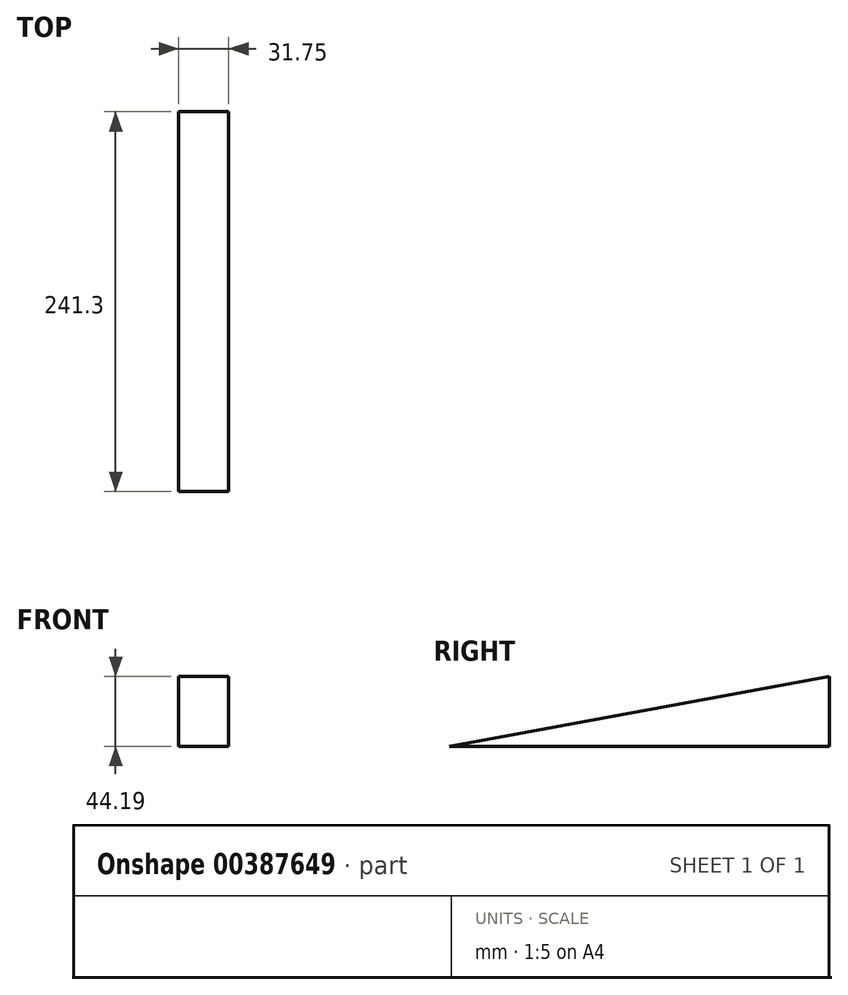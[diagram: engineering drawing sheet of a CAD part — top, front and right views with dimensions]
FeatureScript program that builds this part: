
annotation { "Feature Type Name" : "Feature", "Feature Type Description" : "" }
export const myFeature = defineFeature(function(context is Context, id is Id, definition is map)
    precondition{}
    {
        {
            var Q0;
            Q0=qCreatedBy(makeId("Right.planeOp"),FACE);
            var sketch = newSketch(context, id + "F0", { "sketchPlane" : qUnion([Q0])});
            skLineSegment(sketch, "E0", {"start": v(151.84, 46.52) * mm, "end": v(151.84, 2.33) * mm});
            skLineSegment(sketch, "E1", {"start": v(151.84, 2.33) * mm, "end": v(-89.46, 2.33) * mm});
            skLineSegment(sketch, "E2", {"start": v(-89.46, 2.33) * mm, "end": v(151.84, 46.52) * mm});
            skSolve(sketch);
        }
        {
            var Q0;
            Q0=makeQuery(id+"F0.imprint","IMPRINT",FACE,{"disambiguationData":[TD([[makeQuery(id+"F0.imprint","IMPRINT",EDGE,{"derivedFrom":sQuery(id+"F0.wireOp",EDGE,"E0")}),-1.0]])]});
            extrude(context, id + "F1", {"entities" : qUnion([Q0]), "depth" : 31.75 * mm});
        }
    });
